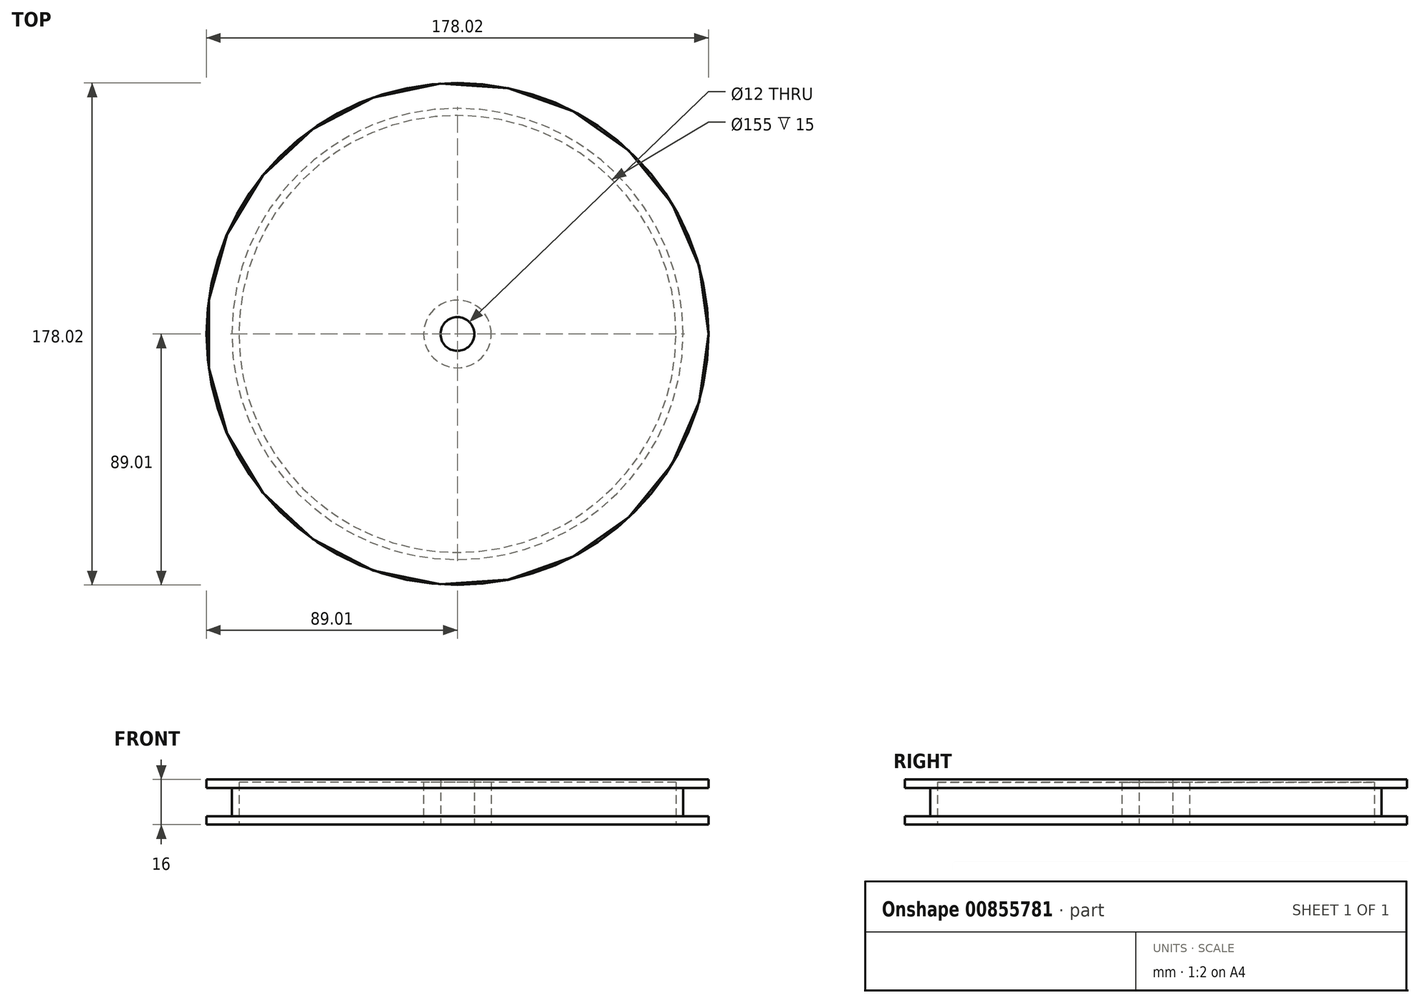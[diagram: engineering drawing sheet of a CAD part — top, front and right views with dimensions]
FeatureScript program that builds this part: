
annotation { "Feature Type Name" : "Feature", "Feature Type Description" : "" }
export const myFeature = defineFeature(function(context is Context, id is Id, definition is map)
    precondition{}
    {
        {
            var Q0;
            Q0=qCreatedBy(makeId("Top.planeOp"),FACE);
            var sketch = newSketch(context, id + "F0", { "sketchPlane" : qUnion([Q0])});
            skCircle(sketch, "E0", {"center": v(0, 0) * mm, "radius": 89 * mm});
            skCircle(sketch, "E1", {"center": v(0, 0) * mm, "radius": 6 * mm});
            skCircle(sketch, "E2", {"center": v(0, 0) * mm, "radius": 80 * mm});
            skCircle(sketch, "E3", {"center": v(0, 0) * mm, "radius": 12 * mm});
            skCircle(sketch, "E4", {"center": v(0, 0) * mm, "radius": 77.5 * mm});
            skSolve(sketch);
        }
        {
            var Q0;
            Q0=makeQuery(id+"F0.imprint","IMPRINT",FACE,{"disambiguationData":[TD([[makeQuery(id+"F0.imprint","IMPRINT",EDGE,{"derivedFrom":sQuery(id+"F0.wireOp",EDGE,"E1")}),-1.0]])]});
            var Q1;
            Q1=makeQuery(id+"F0.imprint","IMPRINT",FACE,{"disambiguationData":[TD([[makeQuery(id+"F0.imprint","IMPRINT",EDGE,{"derivedFrom":sQuery(id+"F0.wireOp",EDGE,"E0")}),1.0]])]});
            var Q2;
            Q2=makeQuery(id+"F0.imprint","IMPRINT",FACE,{"disambiguationData":[TD([[makeQuery(id+"F0.imprint","IMPRINT",EDGE,{"derivedFrom":sQuery(id+"F0.wireOp",EDGE,"E3")}),-1.0]])]});
            var Q3;
            Q3=makeQuery(id+"F0.imprint","IMPRINT",FACE,{"disambiguationData":[TD([[makeQuery(id+"F0.imprint","IMPRINT",EDGE,{"derivedFrom":sQuery(id+"F0.wireOp",EDGE,"E2")}),1.0]])]});
            extrude(context, id + "F1", {"entities" : qUnion([Q0, Q1, Q2, Q3]), "depth" : 16 * mm, "offsetDistance" : 25 * mm});
        }
        {
            var Q0;
            Q0=qCreatedBy(makeId("Front.planeOp"),FACE);
            var sketch = newSketch(context, id + "F2", { "sketchPlane" : qUnion([Q0])});
            skLineSegment(sketch, "E5.bottom", {"start": v(-89, 3) * mm, "end": v(-80, 3) * mm});
            skLineSegment(sketch, "E5.top", {"start": v(-89, 13) * mm, "end": v(-80, 13) * mm});
            skLineSegment(sketch, "E5.left", {"start": v(-89, 3) * mm, "end": v(-89, 13) * mm});
            skLineSegment(sketch, "E5.right", {"start": v(-80, 3) * mm, "end": v(-80, 13) * mm});
            skLineSegment(sketch, "E6", {"start": v(0, 0) * mm, "end": v(0, 31.3) * mm});
            skSolve(sketch);
        }
        {
            var Q0;
            Q0=makeQuery(id+"F2.imprint","IMPRINT",FACE,{"disambiguationData":[TD([[makeQuery(id+"F2.imprint","IMPRINT",EDGE,{"derivedFrom":sQuery(id+"F2.wireOp",EDGE,"E5.bottom")}),1.0]])]});
            var Q1;
            Q1=sQuery(id+"F2.wireOp",EDGE,"E6");
            revolve(context, id + "F3", {"operationType" : NewBodyOperationType.REMOVE, "surfaceOperationType" : NewSurfaceOperationType.NEW, "entities" : qUnion([Q0]), "axis" : qUnion([Q1]), "revolveType" : RevolveType.FULL, "oppositeDirection" : true});
        }
        {
            var Q0;
            Q0=makeQuery(id+"F0.imprint","IMPRINT",FACE,{"disambiguationData":[TD([[makeQuery(id+"F0.imprint","IMPRINT",EDGE,{"derivedFrom":sQuery(id+"F0.wireOp",EDGE,"E3")}),-1.0]])]});
            extrude(context, id + "F4", {"entities" : qUnion([Q0]), "operationType" : NewBodyOperationType.REMOVE, "depth" : 15 * mm, "offsetDistance" : 25 * mm});
        }
    });
